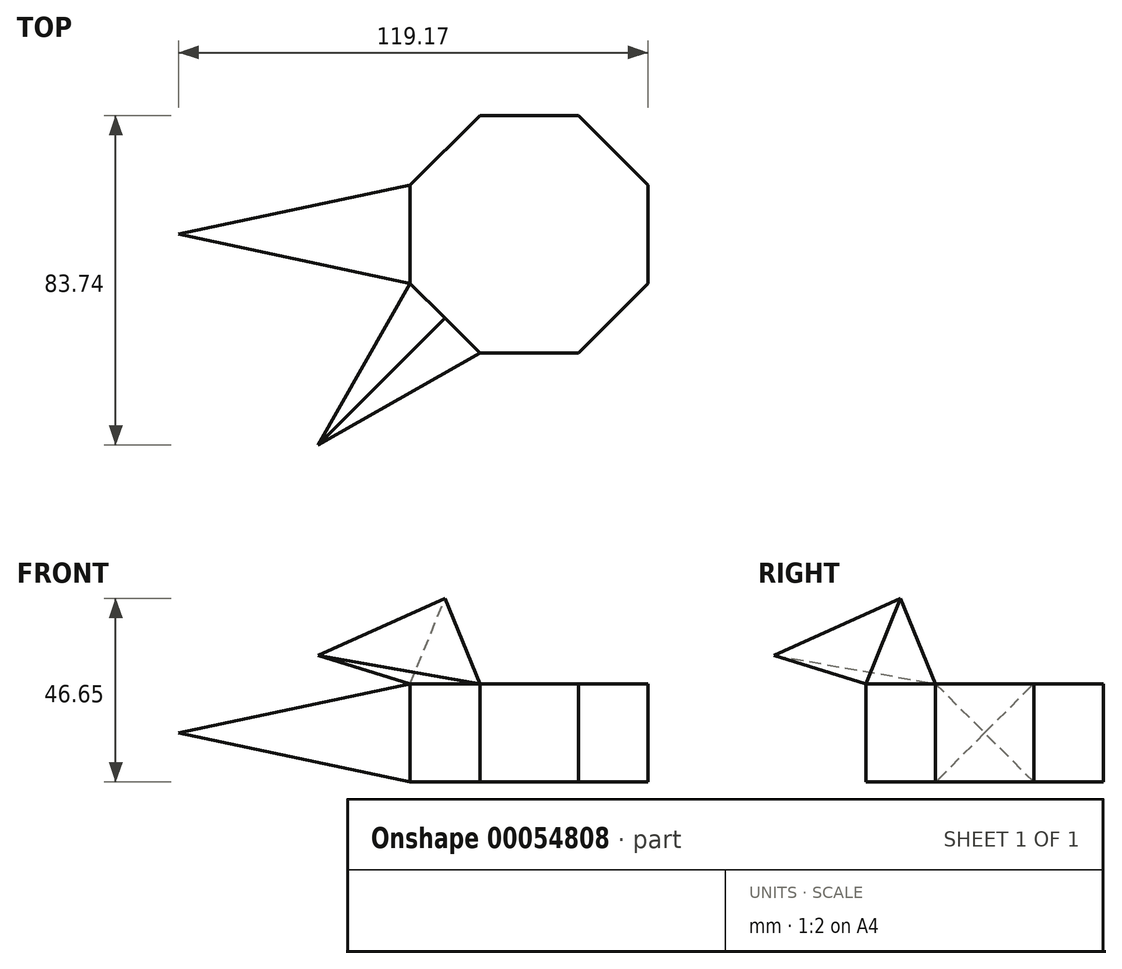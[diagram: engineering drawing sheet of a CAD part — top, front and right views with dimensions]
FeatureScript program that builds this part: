
annotation { "Feature Type Name" : "Feature", "Feature Type Description" : "" }
export const myFeature = defineFeature(function(context is Context, id is Id, definition is map)
    precondition{}
    {
        {
            var Q0;
            Q0=qCreatedBy(makeId("Top.planeOp"),FACE);
            var sketch = newSketch(context, id + "F0", { "sketchPlane" : qUnion([Q0])});
            skCircle(sketch, "E0.cCircle", {"center": v(0, 0) * mm, "radius": 30.18 * mm, "construction": true});
            skLineSegment(sketch, "E0.0", {"start": v(30.18, -12.5) * mm, "end": v(12.5, -30.18) * mm});
            skLineSegment(sketch, "E0.1", {"start": v(12.5, -30.18) * mm, "end": v(-12.5, -30.18) * mm});
            skLineSegment(sketch, "E0.2", {"start": v(-12.5, -30.18) * mm, "end": v(-30.18, -12.5) * mm});
            skLineSegment(sketch, "E0.3", {"start": v(-30.18, -12.5) * mm, "end": v(-30.18, 12.5) * mm});
            skLineSegment(sketch, "E0.4", {"start": v(-30.18, 12.5) * mm, "end": v(-12.5, 30.18) * mm});
            skLineSegment(sketch, "E0.5", {"start": v(-12.5, 30.18) * mm, "end": v(12.5, 30.18) * mm});
            skLineSegment(sketch, "E0.6", {"start": v(12.5, 30.18) * mm, "end": v(30.18, 12.5) * mm});
            skLineSegment(sketch, "E0.7", {"start": v(30.18, 12.5) * mm, "end": v(30.18, -12.5) * mm});
            skPoint(sketch, "E0.0.midPoint", {"position": v(21.34, -21.34) * mm});
            skSolve(sketch);
        }
        {
            var Q0;
            Q0=makeQuery(id+"F0.imprint","IMPRINT",FACE,{"disambiguationData":[TD([[makeQuery(id+"F0.imprint","IMPRINT",EDGE,{"derivedFrom":sQuery(id+"F0.wireOp",EDGE,"E0.0")}),-1.0]])]});
            extrude(context, id + "F1", {"entities" : qUnion([Q0]), "depth" : 25 * mm});
        }
        {
            var Q0;
            Q0=makeQuery(id+"F1.opExtrude","SWEPT_FACE",FACE,{"disambiguationData":[OSD([sQuery(id+"F0.wireOp",EDGE,"E0.3")])]});
            extrude(context, id + "F2", {"entities" : qUnion([Q0]), "depth" : 59 * mm, "hasDraft" : true, "draftAngle" : 12 * degree, "draftPullDirection" : true});
        }
        {
            var Q0;
            Q0=makeQuery(id+"F1.opExtrude","SWEPT_FACE",FACE,{"disambiguationData":[OSD([sQuery(id+"F0.wireOp",EDGE,"E0.2")])]});
            var sketch = newSketch(context, id + "F3", { "sketchPlane" : qUnion([Q0])});
            skLineSegment(sketch, "E1.0", {"start": v(12.5, 25) * mm, "end": v(-12.5, 25) * mm});
            skCircle(sketch, "E2.cCircle", {"center": v(0, 32.22) * mm, "radius": 7.22 * mm, "construction": true});
            skLineSegment(sketch, "E2.1", {"start": v(-12.5, 25) * mm, "end": v(0, 46.65) * mm});
            skLineSegment(sketch, "E2.2", {"start": v(0, 46.65) * mm, "end": v(12.5, 25) * mm});
            skPoint(sketch, "E2.0.midPoint", {"position": v(0, 25) * mm});
            skSolve(sketch);
        }
        {
            var Q0;
            Q0=makeQuery(id+"F3.imprint","IMPRINT",FACE,{"disambiguationData":[TD([[makeQuery(id+"F3.imprint","IMPRINT",EDGE,{"derivedFrom":sQuery(id+"F3.wireOp",EDGE,"E1.0")}),-1.0]])]});
            extrude(context, id + "F4", {"entities" : qUnion([Q0]), "depth" : 59 * mm, "hasDraft" : true, "draftAngle" : 9 * degree, "draftPullDirection" : true});
        }
    });
